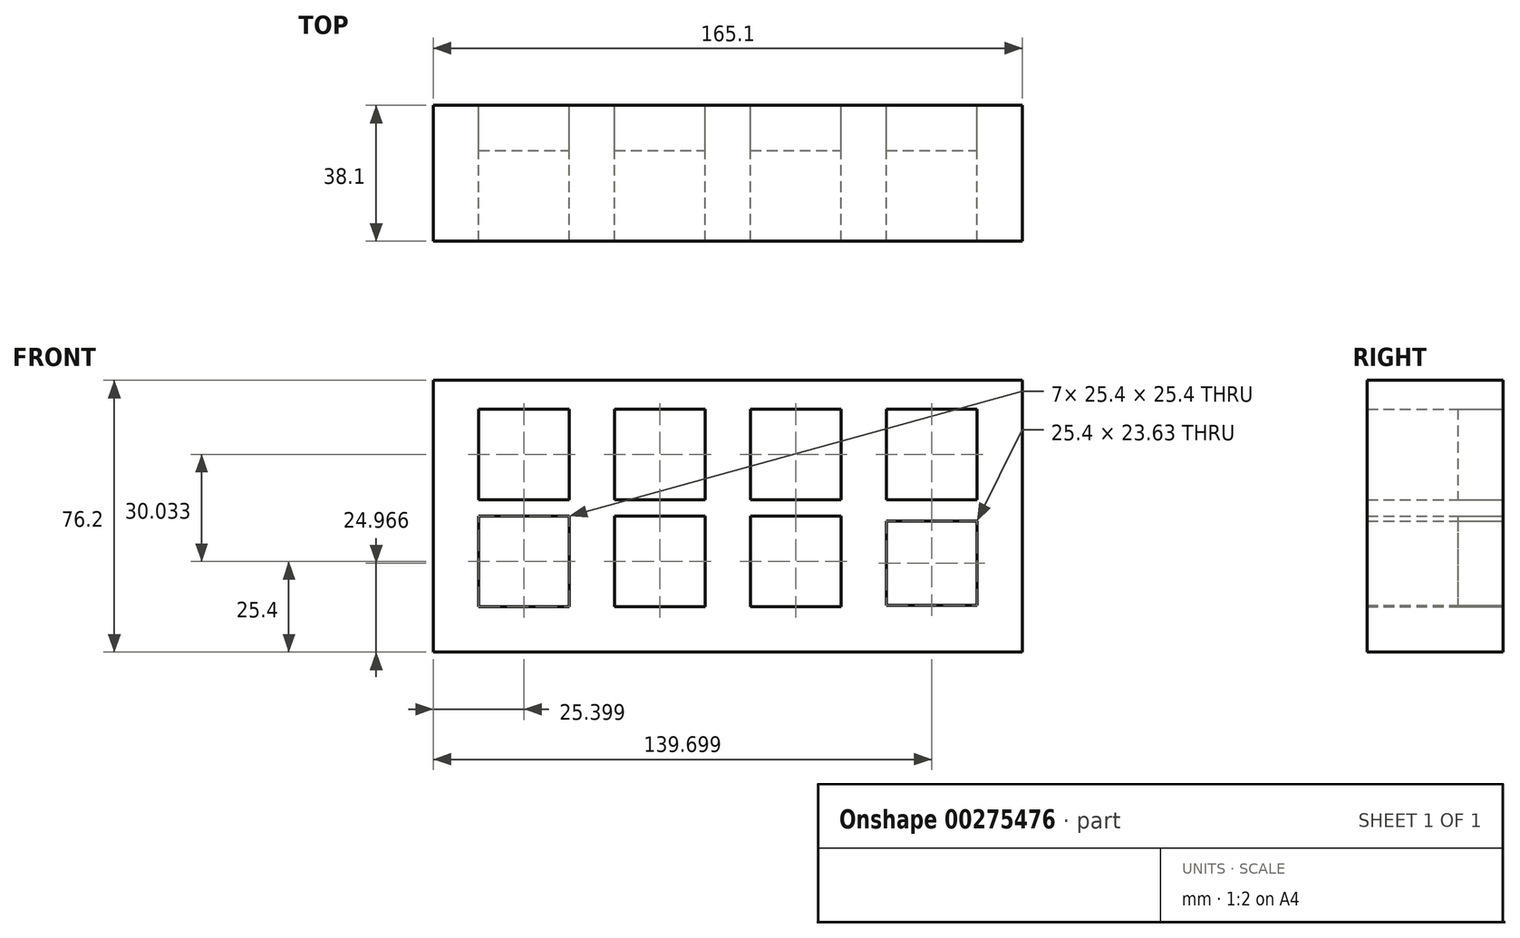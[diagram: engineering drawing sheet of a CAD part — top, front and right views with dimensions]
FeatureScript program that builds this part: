
annotation { "Feature Type Name" : "Feature", "Feature Type Description" : "" }
export const myFeature = defineFeature(function(context is Context, id is Id, definition is map)
    precondition{}
    {
        {
            var Q0;
            Q0=qCreatedBy(makeId("Front.planeOp"),FACE);
            var sketch = newSketch(context, id + "F0", { "sketchPlane" : qUnion([Q0])});
            skLineSegment(sketch, "E0", {"start": v(62.6, 76.2) * mm, "end": v(-102.5, 76.2) * mm});
            skLineSegment(sketch, "E1", {"start": v(62.6, 0) * mm, "end": v(-102.5, 0) * mm});
            skLineSegment(sketch, "E2", {"start": v(-102.5, 76.2) * mm, "end": v(-102.5, 0) * mm});
            skLineSegment(sketch, "E3", {"start": v(62.6, 76.2) * mm, "end": v(62.6, 0) * mm});
            skLineSegment(sketch, "E4", {"start": v(-102.5, 55.43) * mm, "end": v(-77.1, 55.43) * mm, "construction": true});
            skLineSegment(sketch, "E5", {"start": v(-77.1, 55.43) * mm, "end": v(-77.1, 76.2) * mm, "construction": true});
            skLineSegment(sketch, "E6.bottom", {"start": v(-89.8, 68.13) * mm, "end": v(-64.4, 68.13) * mm});
            skLineSegment(sketch, "E6.top", {"start": v(-89.8, 42.73) * mm, "end": v(-64.4, 42.73) * mm});
            skLineSegment(sketch, "E6.left", {"start": v(-89.8, 68.13) * mm, "end": v(-89.8, 42.73) * mm});
            skLineSegment(sketch, "E6.right", {"start": v(-64.4, 68.13) * mm, "end": v(-64.4, 42.73) * mm});
            skPoint(sketch, "E6.middle", {"position": v(-77.1, 55.43) * mm});
            skLineSegment(sketch, "E7", {"start": v(-102.5, 25.4) * mm, "end": v(-77.1, 25.4) * mm});
            skLineSegment(sketch, "E8", {"start": v(-77.1, 25.4) * mm, "end": v(-77.1, 0) * mm});
            skLineSegment(sketch, "E9.bottom", {"start": v(-89.8, 38.1) * mm, "end": v(-64.4, 38.1) * mm});
            skLineSegment(sketch, "E9.top", {"start": v(-89.8, 12.7) * mm, "end": v(-64.4, 12.7) * mm});
            skLineSegment(sketch, "E9.left", {"start": v(-89.8, 38.1) * mm, "end": v(-89.8, 12.7) * mm});
            skLineSegment(sketch, "E9.right", {"start": v(-64.4, 38.1) * mm, "end": v(-64.4, 12.7) * mm});
            skPoint(sketch, "E9.middle", {"position": v(-77.1, 25.4) * mm});
            skLineSegment(sketch, "E10", {"start": v(-77.1, 55.43) * mm, "end": v(-39, 55.43) * mm});
            skLineSegment(sketch, "E11.bottom", {"start": v(-51.7, 68.13) * mm, "end": v(-26.3, 68.13) * mm});
            skLineSegment(sketch, "E11.top", {"start": v(-51.7, 42.73) * mm, "end": v(-26.3, 42.73) * mm});
            skLineSegment(sketch, "E11.left", {"start": v(-51.7, 68.13) * mm, "end": v(-51.7, 42.73) * mm});
            skLineSegment(sketch, "E11.right", {"start": v(-26.3, 68.13) * mm, "end": v(-26.3, 42.73) * mm});
            skPoint(sketch, "E11.middle", {"position": v(-39, 55.43) * mm});
            skLineSegment(sketch, "E12", {"start": v(-77.1, 25.4) * mm, "end": v(-39, 25.4) * mm});
            skLineSegment(sketch, "E13.bottom", {"start": v(-51.7, 38.1) * mm, "end": v(-26.3, 38.1) * mm});
            skLineSegment(sketch, "E13.top", {"start": v(-51.7, 12.7) * mm, "end": v(-26.3, 12.7) * mm});
            skLineSegment(sketch, "E13.left", {"start": v(-51.7, 38.1) * mm, "end": v(-51.7, 12.7) * mm});
            skLineSegment(sketch, "E13.right", {"start": v(-26.3, 38.1) * mm, "end": v(-26.3, 12.7) * mm});
            skPoint(sketch, "E13.middle", {"position": v(-39, 25.4) * mm});
            skLineSegment(sketch, "E14", {"start": v(-39, 55.43) * mm, "end": v(-0.9, 55.43) * mm});
            skLineSegment(sketch, "E15", {"start": v(-39, 25.4) * mm, "end": v(-0.9, 25.4) * mm});
            skLineSegment(sketch, "E16.bottom", {"start": v(-13.6, 68.13) * mm, "end": v(11.8, 68.13) * mm});
            skLineSegment(sketch, "E16.top", {"start": v(-13.6, 42.73) * mm, "end": v(11.8, 42.73) * mm});
            skLineSegment(sketch, "E16.left", {"start": v(-13.6, 68.13) * mm, "end": v(-13.6, 42.73) * mm});
            skLineSegment(sketch, "E16.right", {"start": v(11.8, 68.13) * mm, "end": v(11.8, 42.73) * mm});
            skPoint(sketch, "E16.middle", {"position": v(-0.9, 55.43) * mm});
            skLineSegment(sketch, "E17.bottom", {"start": v(-13.6, 38.1) * mm, "end": v(11.8, 38.1) * mm});
            skLineSegment(sketch, "E17.top", {"start": v(-13.6, 12.7) * mm, "end": v(11.8, 12.7) * mm});
            skLineSegment(sketch, "E17.left", {"start": v(-13.6, 38.1) * mm, "end": v(-13.6, 12.7) * mm});
            skLineSegment(sketch, "E17.right", {"start": v(11.8, 38.1) * mm, "end": v(11.8, 12.7) * mm});
            skPoint(sketch, "E17.middle", {"position": v(-0.9, 25.4) * mm});
            skLineSegment(sketch, "E18", {"start": v(-0.9, 55.43) * mm, "end": v(37.2, 55.43) * mm});
            skLineSegment(sketch, "E19", {"start": v(-0.9, 25.4) * mm, "end": v(37.2, 25.4) * mm});
            skLineSegment(sketch, "E20.bottom", {"start": v(24.5, 68.13) * mm, "end": v(49.9, 68.13) * mm});
            skLineSegment(sketch, "E20.top", {"start": v(24.5, 42.73) * mm, "end": v(49.9, 42.73) * mm});
            skLineSegment(sketch, "E20.left", {"start": v(24.5, 68.13) * mm, "end": v(24.5, 42.73) * mm});
            skLineSegment(sketch, "E20.right", {"start": v(49.9, 68.13) * mm, "end": v(49.9, 42.73) * mm});
            skPoint(sketch, "E20.middle", {"position": v(37.2, 55.43) * mm});
            skLineSegment(sketch, "E21.bottom", {"start": v(24.5, 36.78) * mm, "end": v(49.9, 36.78) * mm});
            skLineSegment(sketch, "E21.top", {"start": v(24.5, 13.15) * mm, "end": v(49.9, 13.15) * mm});
            skLineSegment(sketch, "E21.left", {"start": v(24.5, 36.78) * mm, "end": v(24.5, 13.15) * mm});
            skLineSegment(sketch, "E21.right", {"start": v(49.9, 36.78) * mm, "end": v(49.9, 13.15) * mm});
            skPoint(sketch, "E21.middle", {"position": v(37.2, 24.97) * mm});
            skLineSegment(sketch, "E22", {"start": v(37.2, 55.43) * mm, "end": v(37.2, 76.2) * mm});
            skLineSegment(sketch, "E23", {"start": v(62.6, 55.43) * mm, "end": v(37.2, 55.43) * mm});
            skLineSegment(sketch, "E24", {"start": v(62.6, 55.43) * mm, "end": v(62.6, 55.43) * mm});
            skSolve(sketch);
        }
        {
            var Q0;
            {var subQ45=sQuery(id+"F0.wireOp",EDGE,"E6.bottom");Q0=makeQuery(id+"F0.imprint","IMPRINT",FACE,{"disambiguationData":[TD([[makeQuery(id+"F0.imprint","IMPRINT",EDGE,{"derivedFrom":subQ45}),1.0]])]});}
            var Q1;
            {var subQ1=sQuery(id+"F0.wireOp",EDGE,"E2");var subQ5=sQuery(id+"F0.wireOp",EDGE,"E1");var subQ6=makeQuery(id+"F0.imprint","INTERSECT",VERTEX,{"derivedFrom":[subQ5,subQ1]});Q1=makeQuery(id+"F0.imprint","IMPRINT",FACE,{"disambiguationData":[TD([[makeQuery(id+"F0.imprint","IMPRINT",EDGE,{"disambiguationData":[TD([[subQ6,1.0]])],"derivedFrom":subQ5}),-1.0]])]});}
            var Q2;
            {var subQ7=sQuery(id+"F0.wireOp",EDGE,"E3");var subQ8=sQuery(id+"F0.wireOp",EDGE,"E0");var subQ9=makeQuery(id+"F0.imprint","INTERSECT",VERTEX,{"derivedFrom":[subQ8,subQ7]});Q2=makeQuery(id+"F0.imprint","IMPRINT",FACE,{"disambiguationData":[TD([[makeQuery(id+"F0.imprint","IMPRINT",EDGE,{"disambiguationData":[TD([[subQ9,-1.0]])],"derivedFrom":subQ8}),1.0]])]});}
            extrude(context, id + "F1", {"entities" : qUnion([Q0, Q1, Q2]), "depth" : 38.1 * mm});
        }
        {
            var Q0;
            {var subQ1=sQuery(id+"F0.wireOp",EDGE,"E6.bottom");Q0=makeQuery(id+"F0.imprint","IMPRINT",FACE,{"disambiguationData":[TD([[makeQuery(id+"F0.imprint","IMPRINT",EDGE,{"derivedFrom":subQ1}),-1.0]])]});}
            var Q1;
            {var subQ3=sQuery(id+"F0.wireOp",EDGE,"E9.top");var subQ5=sQuery(id+"F0.wireOp",EDGE,"E9.right");var subQ6=makeQuery(id+"F0.imprint","INTERSECT",VERTEX,{"derivedFrom":[subQ3,subQ5]});Q1=makeQuery(id+"F0.imprint","IMPRINT",FACE,{"disambiguationData":[TD([[makeQuery(id+"F0.imprint","IMPRINT",EDGE,{"disambiguationData":[TD([[subQ6,1.0]])],"derivedFrom":subQ3}),1.0]])]});}
            var Q2;
            {var subQ1=sQuery(id+"F0.wireOp",EDGE,"E9.bottom");Q2=makeQuery(id+"F0.imprint","IMPRINT",FACE,{"disambiguationData":[TD([[makeQuery(id+"F0.imprint","IMPRINT",EDGE,{"derivedFrom":subQ1}),-1.0]])]});}
            var Q3;
            {var subQ3=sQuery(id+"F0.wireOp",EDGE,"E9.left");var subQ5=sQuery(id+"F0.wireOp",EDGE,"E9.top");var subQ7=makeQuery(id+"F0.imprint","INTERSECT",VERTEX,{"derivedFrom":[subQ5,subQ3]});Q3=makeQuery(id+"F0.imprint","IMPRINT",FACE,{"disambiguationData":[TD([[makeQuery(id+"F0.imprint","IMPRINT",EDGE,{"disambiguationData":[TD([[subQ7,-1.0]])],"derivedFrom":subQ5}),1.0]])]});}
            var Q4;
            {var subQ1=sQuery(id+"F0.wireOp",EDGE,"E13.top");Q4=makeQuery(id+"F0.imprint","IMPRINT",FACE,{"disambiguationData":[TD([[makeQuery(id+"F0.imprint","IMPRINT",EDGE,{"derivedFrom":subQ1}),1.0]])]});}
            var Q5;
            {var subQ1=sQuery(id+"F0.wireOp",EDGE,"E13.bottom");Q5=makeQuery(id+"F0.imprint","IMPRINT",FACE,{"disambiguationData":[TD([[makeQuery(id+"F0.imprint","IMPRINT",EDGE,{"derivedFrom":subQ1}),-1.0]])]});}
            var Q6;
            {var subQ1=sQuery(id+"F0.wireOp",EDGE,"E11.top");Q6=makeQuery(id+"F0.imprint","IMPRINT",FACE,{"disambiguationData":[TD([[makeQuery(id+"F0.imprint","IMPRINT",EDGE,{"derivedFrom":subQ1}),1.0]])]});}
            var Q7;
            {var subQ1=sQuery(id+"F0.wireOp",EDGE,"E11.bottom");Q7=makeQuery(id+"F0.imprint","IMPRINT",FACE,{"disambiguationData":[TD([[makeQuery(id+"F0.imprint","IMPRINT",EDGE,{"derivedFrom":subQ1}),-1.0]])]});}
            var Q8;
            {var subQ1=sQuery(id+"F0.wireOp",EDGE,"E17.top");Q8=makeQuery(id+"F0.imprint","IMPRINT",FACE,{"disambiguationData":[TD([[makeQuery(id+"F0.imprint","IMPRINT",EDGE,{"derivedFrom":subQ1}),1.0]])]});}
            var Q9;
            {var subQ1=sQuery(id+"F0.wireOp",EDGE,"E17.bottom");Q9=makeQuery(id+"F0.imprint","IMPRINT",FACE,{"disambiguationData":[TD([[makeQuery(id+"F0.imprint","IMPRINT",EDGE,{"derivedFrom":subQ1}),-1.0]])]});}
            var Q10;
            {var subQ1=sQuery(id+"F0.wireOp",EDGE,"E16.bottom");Q10=makeQuery(id+"F0.imprint","IMPRINT",FACE,{"disambiguationData":[TD([[makeQuery(id+"F0.imprint","IMPRINT",EDGE,{"derivedFrom":subQ1}),-1.0]])]});}
            var Q11;
            {var subQ1=sQuery(id+"F0.wireOp",EDGE,"E16.top");Q11=makeQuery(id+"F0.imprint","IMPRINT",FACE,{"disambiguationData":[TD([[makeQuery(id+"F0.imprint","IMPRINT",EDGE,{"derivedFrom":subQ1}),1.0]])]});}
            var Q12;
            {var subQ1=sQuery(id+"F0.wireOp",EDGE,"E20.top");Q12=makeQuery(id+"F0.imprint","IMPRINT",FACE,{"disambiguationData":[TD([[makeQuery(id+"F0.imprint","IMPRINT",EDGE,{"derivedFrom":subQ1}),1.0]])]});}
            var Q13;
            {var subQ3=sQuery(id+"F0.wireOp",EDGE,"E20.left");var subQ5=sQuery(id+"F0.wireOp",EDGE,"E20.bottom");var subQ6=makeQuery(id+"F0.imprint","INTERSECT",VERTEX,{"derivedFrom":[subQ5,subQ3]});Q13=makeQuery(id+"F0.imprint","IMPRINT",FACE,{"disambiguationData":[TD([[makeQuery(id+"F0.imprint","IMPRINT",EDGE,{"disambiguationData":[TD([[subQ6,-1.0]])],"derivedFrom":subQ5}),-1.0]])]});}
            var Q14;
            {var subQ0=sQuery(id+"F0.wireOp",EDGE,"E20.right");var subQ1=sQuery(id+"F0.wireOp",EDGE,"E20.bottom");var subQ2=makeQuery(id+"F0.imprint","INTERSECT",VERTEX,{"derivedFrom":[subQ1,subQ0]});Q14=makeQuery(id+"F0.imprint","IMPRINT",FACE,{"disambiguationData":[TD([[makeQuery(id+"F0.imprint","IMPRINT",EDGE,{"disambiguationData":[TD([[subQ2,1.0]])],"derivedFrom":subQ1}),-1.0]])]});}
            var Q15;
            {var subQ3=sQuery(id+"F0.wireOp",EDGE,"E21.bottom");Q15=makeQuery(id+"F0.imprint","IMPRINT",FACE,{"disambiguationData":[TD([[makeQuery(id+"F0.imprint","IMPRINT",EDGE,{"derivedFrom":subQ3}),-1.0]])]});}
            extrude(context, id + "F2", {"entities" : qUnion([Q0, Q1, Q2, Q3, Q4, Q5, Q6, Q7, Q8, Q9, Q10, Q11, Q12, Q13, Q14, Q15]), "depth" : 12.7 * mm});
        }
    });
